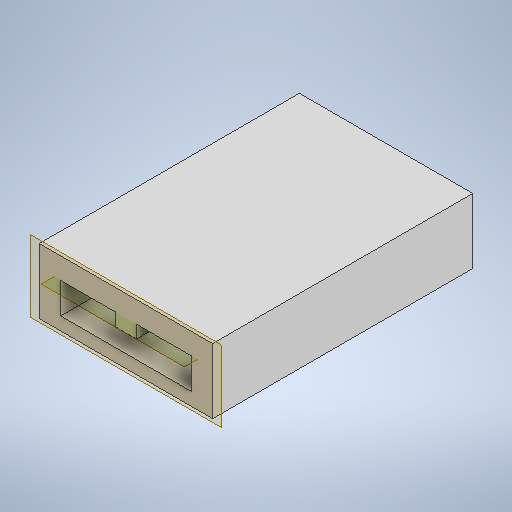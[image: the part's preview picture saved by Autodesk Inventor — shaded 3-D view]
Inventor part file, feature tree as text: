
AUTODESK INVENTOR PART (.ipt)
format: ipt  version: 2025.1 (Build 291241000, 241)  size: 237,568 bytes
history: native  units: mm
features: other x3, extrude x3, sketch x3
ambient origin geometry x8: Origin, YZ Plane, XZ Plane, XY Plane, X Axis, Y Axis, Z Axis, Center Point
bodies: Body1 (feature_tree)
feature tree (9):
  other  "ソリッド1"
  extrude  "押し出し1"  Depth=40.0mm
  other  "作業平面1"
  extrude  "押し出し2"  Depth=60.0mm
  other  "作業平面2"
  extrude  "押し出し3"  Depth=15.0mm TaperAngle=0.0deg
  sketch  "スケッチ1"
  sketch  "スケッチ2"
  sketch  "スケッチ3"
